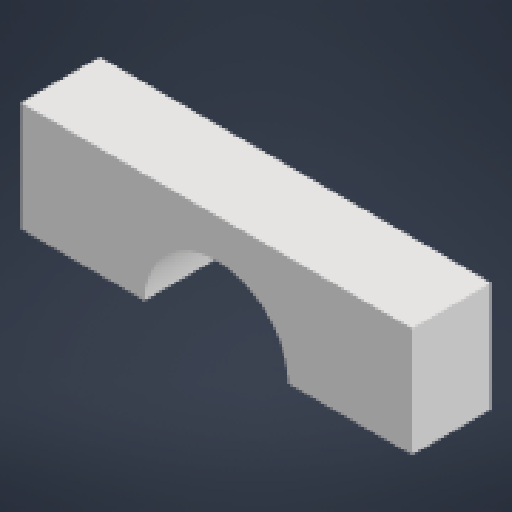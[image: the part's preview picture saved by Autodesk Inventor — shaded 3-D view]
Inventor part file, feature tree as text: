
AUTODESK INVENTOR PART (.ipt)
format: ipt  version: 2023.2 (Build 272271000, 271)  size: 119,296 bytes
history: native  units: mm
features: other x3, sketch x2, extrude x2, reference x2, plane x1
ambient origin geometry x8: Origin, YZ Plane, XZ Plane, XY Plane, X Axis, Y Axis, Z Axis, Center Point
bodies: Solid1 (feature_tree)
feature tree (10):
  sketch  "Sketch1"  dims[d0=10.0mm d1=0.0mm d2=0.0mm d3=0.0mm]
  plane  "Work Plane1"
  extrude  "Extrusion1"  TaperAngle=0.0deg  [1 undecoded]
  extrude  "Extrusion2"  [1 undecoded]
  sketch  "Sketch2"
  reference  "Reference2"
  reference  "Reference3"
  parser-record x1  (decoder bookkeeping rows leaked as tree rows — omitted from the tree; the rows remain in map.json)
  other  "turret_assembly.iam"
  other  "pylon_actuator_holder:2"
note: 2 required parameter values undecoded (feature->parameter linkage not recoverable at this tier; creation-order binding heuristic only, values carry confidence <= 0.55)
note: 1 file-system path scrubbed to <path> (originals preserved in map.json)
